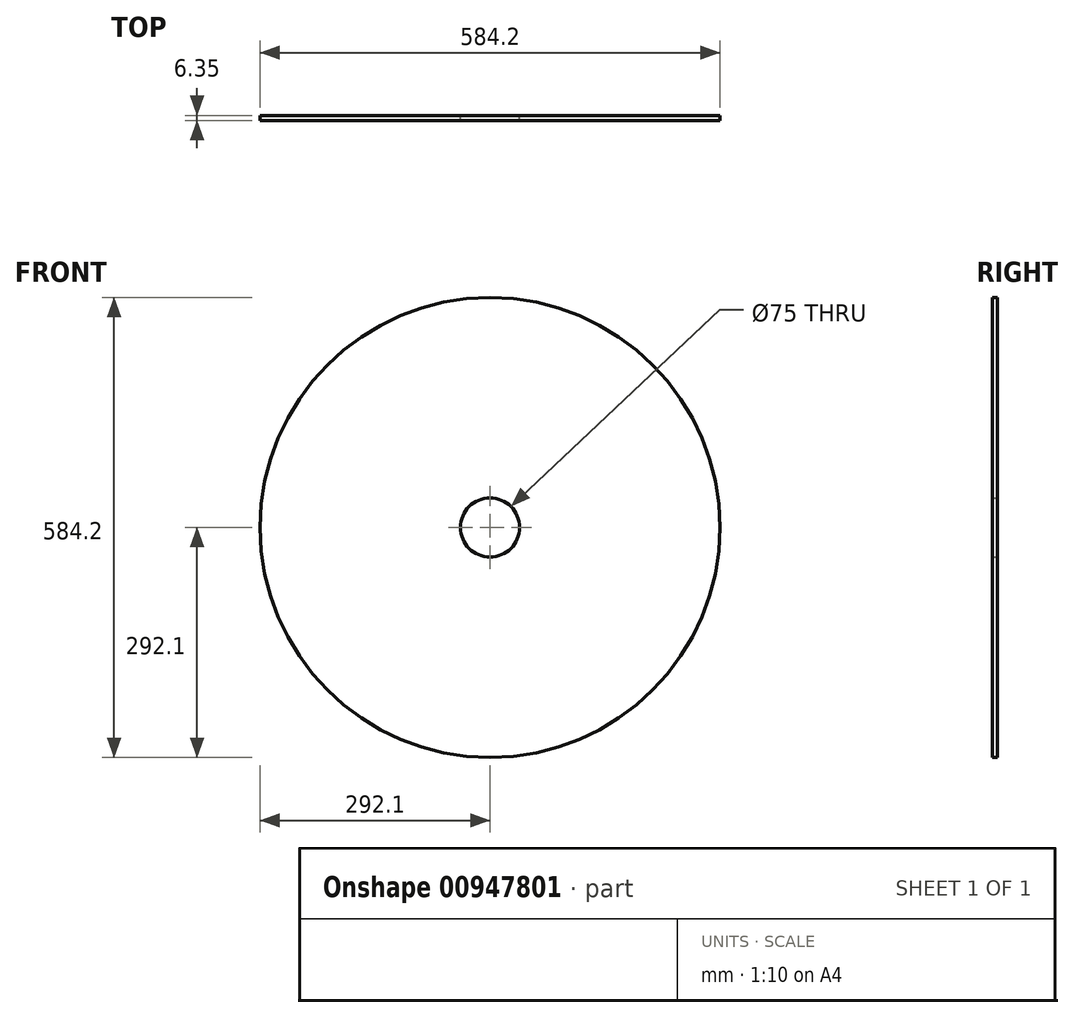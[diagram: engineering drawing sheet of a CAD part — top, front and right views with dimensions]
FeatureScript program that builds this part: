
annotation { "Feature Type Name" : "Feature", "Feature Type Description" : "" }
export const myFeature = defineFeature(function(context is Context, id is Id, definition is map)
    precondition{}
    {
        {
            var Q0;
            Q0=qCreatedBy(makeId("Front.planeOp"),FACE);
            var sketch = newSketch(context, id + "F0", { "sketchPlane" : qUnion([Q0])});
            skCircle(sketch, "E0", {"center": v(0, 0) * mm, "radius": 292.1 * mm});
            skCircle(sketch, "E1", {"center": v(0, 0) * mm, "radius": 37.5 * mm});
            skSolve(sketch);
        }
        {
            var Q0;
            Q0 = qSketchRegion(id + "F0", true);
            extrude(context, id + "F1", {"entities" : qUnion([Q0]), "depth" : 6.35 * mm, "offsetDistance" : 25 * mm});
        }
    });
